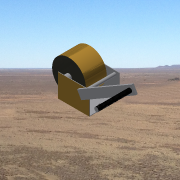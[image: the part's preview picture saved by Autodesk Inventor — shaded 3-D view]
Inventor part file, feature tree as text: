
AUTODESK INVENTOR PART (.ipt)
format: ipt  version: 2013 SP2 (Build 170200200, 200)  size: 212,480 bytes
history: native  units: in
note: dims shown in document units (in); Inventor stores cm internally (conversion verified against a paired STEP export)
features: sketch x9, extrude x8, hole x1
ambient origin geometry x8: Origin, YZ Plane, XZ Plane, XY Plane, X Axis, Y Axis, Z Axis, Center Point
bodies: Solid1 (feature_tree)
feature tree (18):
  extrude  "Extrusion1"  Depth=2.5in TaperAngle=0.0deg
  extrude  "Extrusion2"  Depth=0.625in TaperAngle=0.0deg
  extrude  "Extrusion3"  Depth=2.75in
  extrude  "Extrusion4"  Depth=0.06in
  extrude  "Extrusion5"  Depth=0.06in TaperAngle=0.0deg
  extrude  "Extrusion6"  Depth=0.5in TaperAngle=0.0deg
  extrude  "Extrusion7"  Depth=7.5in
  extrude  "Extrusion8"  Depth=0.25in TaperAngle=0.0deg
  hole  "Hole1"  [1 undecoded]
  sketch  "Sketch1"  dims[d0=4.0in d2=2.5in d3=0.0in]
  sketch  "Sketch2"  dims[d5=0.75in d7=0.625in d8=3.0in d9=0.0in d10=0.0in]
  sketch  "Sketch3"  dims[d11=3.75in d13=2.75in]
  sketch  "Sketch4"  dims[d14=0.06in d15=0.0in d16=0.06in]
  sketch  "Sketch5"  dims[d17=3.5in d18=0.0in d19=0.06in d20=0.0in]
  sketch  "Sketch6"  dims[d21=0.375in d23=0.5in d24=3.75in d25=0.0in d26=0.0in]
  sketch  "Sketch7"  dims[d29=1.0in d30=7.5in]
  sketch  "Sketch8"  dims[d40=30.0deg d41=0.25in d42=0.0in]
  sketch  "Sketch9"  dims[d43=0.5in d44=0.5in d45=4.0in d46=0.0in d47=2.75in d48=3.75in d49=3.62in d50=3.75in d51=0.375in d52=0.5in d53=0.7874in d55=2.75in d56=0.3937in d58=1.0in d60=0.375in d61=0.75in d62=0.375in d63=0.25in d64=0.5635in d65=0.1in d66=0.8108in]
note: 1 required parameter value undecoded (feature->parameter linkage not recoverable at this tier; creation-order binding heuristic only, values carry confidence <= 0.55)
